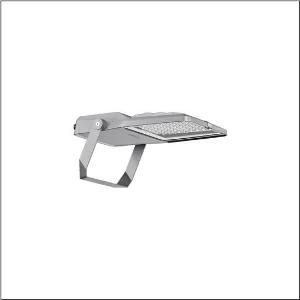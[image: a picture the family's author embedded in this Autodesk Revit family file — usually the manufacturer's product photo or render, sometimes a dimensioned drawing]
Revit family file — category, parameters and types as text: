
# Revit family: floodlight_fl_21_iq_mini___pl61_5xa7772c5c1a_22e4
name_source: partatom
category: Lighting Fixtures
units: mm (PartAtom-declared; Revit-internal decimal feet)

## family parameters
Cut with Voids When Loaded = No
Host = Face
Light Source = No
Part Type = Normal
Room Calculation Point = No
Round Connector Dimension = Use Diameter
Shared = No

## types (1)
- --- (1 x LED, 11180 lm, 87.2 W, 4000K)
    Apparent Load = 87 VA
    CIE Flux Codes = 33 65 98 100 100
    Color Rendering = 80
    Color Temperature = 4000K
    Default Elevation = 1800 mm
    Description = Floodlight FL 21 iQ mini, floodlight, primary light control with lens, of PMMA, primary optical cover: protective disc, of toughened safety glass, transparent, light distribution: PL61, light emission: direct distribution, installation type: surface-mounted, LED, High Power LED, rated luminous flux: 11.180lm, luminous efficacy: 128lm/W, light colour: 840, colour temperature: 4000K, control: Street-Remote, Auto-Match, Temp-Guard, Night-Set, Smart-Wire, Desk-Remote (wireless, voltage-free reading and setting of iQ features in the workshop via application-optimized NFC function/RFID function), optimised constant luminous flux control (CLO 2.0), with terminal, 6-pole, mains connection: 220..240V, AC, 50/60Hz, start of lifetime: 87W, end of service life: 92W, reduction: 40W, luminaire housing, of diecast aluminium, powder-coated, Siteco® metallic grey (DB 702S), corrosivity category C5 mid according to DIN EN ISO 12944, sealing non-destructively replaceable, mounting bracket, of steel, galvanised, powder-coated, Siteco® metallic grey (DB 702S), protection rating (complete): IP66, insulation class (complete): insulation class II (safety insulation), certification: CE, ENEC, VDE, protection symbol: D, impact resistance: IK08, permissible operating ambient temperature: -40..+40°C, permissible operating ambient temperature for outdoor applications: -40..+50°C, standard: DIN EN 12944, LABS conformity tested according to VDMA 24364:2018-05, packaging unit: 1 piece

Light Distribution: PL61
    Height = 70 mm
    Lamp = 1 x LED
    Lamp Light Flux = 11180 lm
    Lamp Power = 87.2 W
    Lamp count = 1
    Length = 485 mm
    Luminous efficacy = 128 lm/W
    Manufacturer = Siteco
    ModVariant = No
    Model = 5XA7772C5C1A
    Number of Poles = 1
    OnlyDefault = Yes
    Power Factor = 1
    Product Name = Floodlight FL 21 iQ mini | PL61
    Product group = floodlight | pylon annexe
    ProductGroupID = 6200
    Protection Class = Protection class II
    Protection Degree = IP 66
    RLX_Detail_Level = 1
    RLX_Emergency_Light_Flux = 0 lm
    RLX_Emergency_Type = 0
    RLX_Emergency_Type_DB = No
    RlxData = <blob elided: 96381 chars, md5=4b08b472>
    Socket = socket
    Standby Power = 0 W
    System Light Flux = 11180 lm
    System Power = 87 W
    Type Comments = factory setting: luminous flux: 100 % | dim-lin: 254 | 456 mA
    Type Image = l_1006845.jpg
    URL = http://relux.com
    VarID = @adj_123791
    Voltage = 0 V
    Weight = 0.00 kg
    Width = 337 mm

## geometry (parser evidence)
native form markers: Blend x4, Sweep x13
no freeform markers — native parametric forms only
